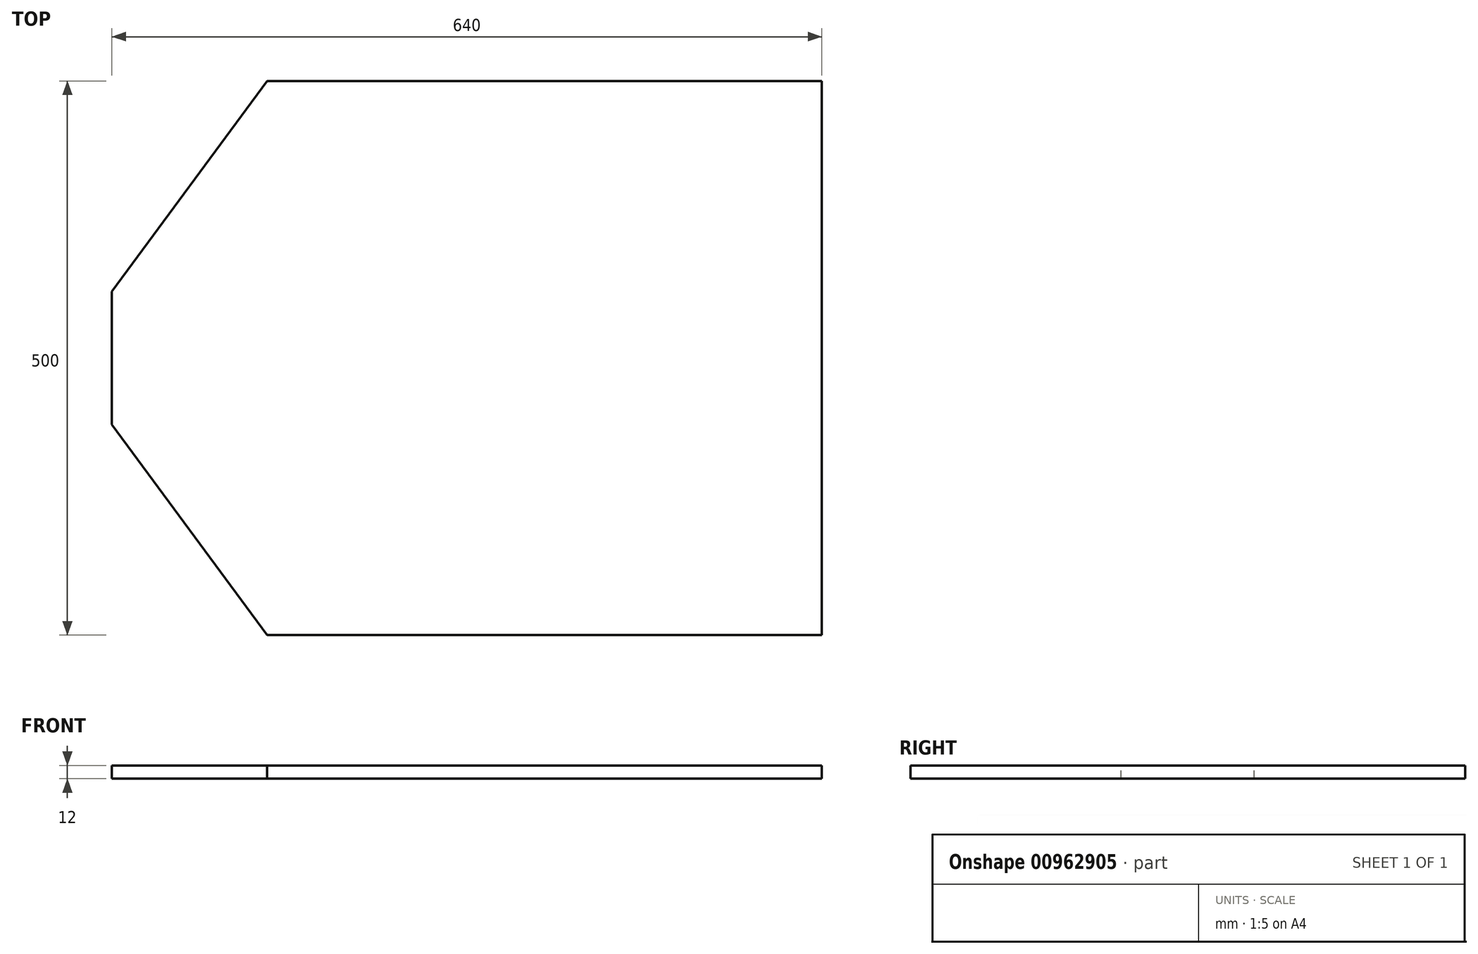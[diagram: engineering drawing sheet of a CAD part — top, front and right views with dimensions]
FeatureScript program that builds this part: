
annotation { "Feature Type Name" : "Feature", "Feature Type Description" : "" }
export const myFeature = defineFeature(function(context is Context, id is Id, definition is map)
    precondition{}
    {
        {
            var Q0;
            Q0=qCreatedBy(makeId("Top.planeOp"),FACE);
            var sketch = newSketch(context, id + "F0", { "sketchPlane" : qUnion([Q0])});
            skLineSegment(sketch, "E0.bottom", {"start": v(-320, 250) * mm, "end": v(320, 250) * mm});
            skLineSegment(sketch, "E0.top", {"start": v(-320, -250) * mm, "end": v(320, -250) * mm});
            skLineSegment(sketch, "E0.left", {"start": v(-320, 250) * mm, "end": v(-320, -250) * mm});
            skLineSegment(sketch, "E0.right", {"start": v(320, 250) * mm, "end": v(320, -250) * mm});
            skPoint(sketch, "E0.middle", {"position": v(0, 0) * mm});
            skLineSegment(sketch, "E1", {"start": v(-320, 250) * mm, "end": v(-320, 21.8) * mm});
            skLineSegment(sketch, "E2", {"start": v(-320, 21.8) * mm, "end": v(-320, -88.2) * mm});
            skLineSegment(sketch, "E3", {"start": v(-320, -88.2) * mm, "end": v(-320, -250) * mm});
            skSolve(sketch);
        }
        {
            var Q0;
            Q0 = qSketchRegion(id + "F0", true);
            extrude(context, id + "F1", {"entities" : qUnion([Q0]), "depth" : 12 * mm, "offsetDistance" : 25 * mm});
        }
        {
            var Q0;
            Q0=makeQuery(id+"F1.opExtrude","CAP_FACE",FACE,{"disambiguationData":[OSD([sQuery(id+"F0.wireOp",EDGE,"E0.bottom"),sQuery(id+"F0.wireOp",EDGE,"E0.top"),sQuery(id+"F0.wireOp",EDGE,"E0.right"),sQuery(id+"F0.wireOp",EDGE,"E1"),sQuery(id+"F0.wireOp",EDGE,"E2"),sQuery(id+"F0.wireOp",EDGE,"E3")])],"isStart":false});
            var sketch = newSketch(context, id + "F2", { "sketchPlane" : qUnion([Q0])});
            skLineSegment(sketch, "E4", {"start": v(320, 250) * mm, "end": v(-180, 250) * mm});
            skLineSegment(sketch, "E5", {"start": v(320, -250) * mm, "end": v(-180, -250) * mm});
            skLineSegment(sketch, "E6", {"start": v(-320, 250) * mm, "end": v(-320, 60) * mm});
            skLineSegment(sketch, "E7", {"start": v(-320, 60) * mm, "end": v(-320, -60) * mm});
            skLineSegment(sketch, "E8", {"start": v(-320, -60) * mm, "end": v(-320, -250) * mm});
            skLineSegment(sketch, "E9", {"start": v(-180, 250) * mm, "end": v(-320, 60) * mm});
            skLineSegment(sketch, "E10", {"start": v(-320, -60) * mm, "end": v(-180, -250) * mm});
            skSolve(sketch);
        }
        {
            var Q0;
            {var subQ0=sQuery(id+"F2.wireOp",EDGE,"E6");Q0=makeQuery(id+"F2.imprint","IMPRINT",FACE,{"disambiguationData":[TD([[makeQuery(id+"F2.imprint","IMPRINT",EDGE,{"derivedFrom":subQ0}),1.0]])]});}
            var Q1;
            {var subQ0=sQuery(id+"F2.wireOp",EDGE,"E8");Q1=makeQuery(id+"F2.imprint","IMPRINT",FACE,{"disambiguationData":[TD([[makeQuery(id+"F2.imprint","IMPRINT",EDGE,{"derivedFrom":subQ0}),1.0]])]});}
            extrude(context, id + "F3", {"entities" : qUnion([Q0, Q1]), "operationType" : NewBodyOperationType.REMOVE, "oppositeDirection" : true, "depth" : 25 * mm, "offsetDistance" : 25 * mm});
        }
    });
